# Revit family: SK-ZONE-6.BIM
name_source: partatom
category: Fire Alarm Devices
units: mm (PartAtom-declared; Revit-internal decimal feet)

## family parameters
Cut with Voids When Loaded = No
Host = Face
Maintain Annotation Orientation = Yes
OmniClass Number = 23.85.30.21
OmniClass Title = Environmental Detection/Registration
Part Type = Normal
Room Calculation Point = No
Round Connector Dimension = Use Diameter
Shared = No

## types (4) — shared parameters
Assembly Code = D5030700
Default Elevation = 4' - 0"
Manufacturer = Silent Knight
Model = SK-ZONE-6
Mounting Requirements = 4 inch square x 2 1/2" deep electrical box.
URL = www.Silent Knight.com

## per-type parameters (varying)
| type | Description | Module Type |
| Monitor | Monitor Module - Standard Size | M |
| Dual Monitor | Monitor Module - Dual Monitor - Standard Size | DM |
| Analog Input | Monitor Module - Analog Input - Standard Size | 4-20 MA |
| Zone Interface | Monitor Module - Zone Interface (2 wire) - Standard Size | Z |

## geometry (parser evidence)
native form markers: Blend x4, Sweep x6
no freeform markers — native parametric forms only
